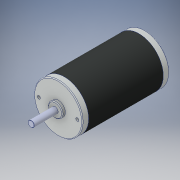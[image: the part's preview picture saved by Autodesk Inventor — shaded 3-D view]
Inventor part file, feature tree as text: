
AUTODESK INVENTOR PART (.ipt)
format: ipt  version: 2016 (Build 200138000, 138)  size: 158,720 bytes
history: native  units: in
note: dims shown in document units (in); Inventor stores cm internally (conversion verified against a paired STEP export)
features: fillet x1
ambient origin geometry x8: Origin, YZ Plane, XZ Plane, XY Plane, X Axis, Y Axis, Z Axis, Center Point
bodies: Solid1 (feature_tree)
feature tree (1):
  fillet  "Fillet4"  [1 undecoded]
note: 1 required parameter value undecoded (feature->parameter linkage not recoverable at this tier; creation-order binding heuristic only, values carry confidence <= 0.55)
